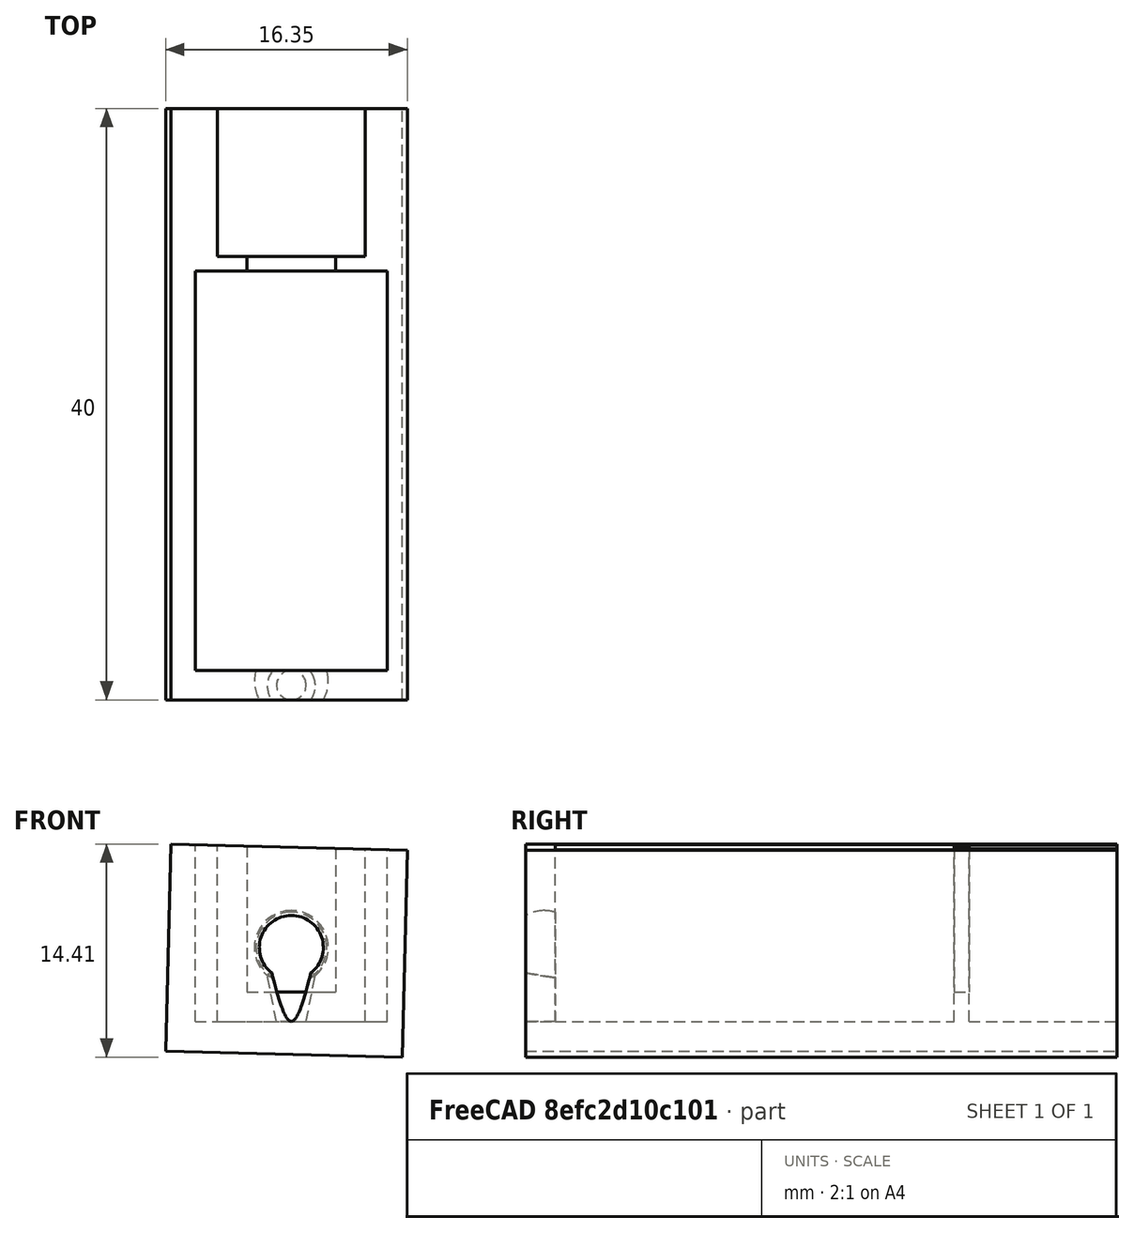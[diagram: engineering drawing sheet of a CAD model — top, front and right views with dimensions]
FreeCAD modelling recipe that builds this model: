
FCSTD DOCUMENT  (FreeCAD 0.16R4924 (Git))
Label: solenoid_bay
License: All rights reserved
LicenseURL: http://en.wikipedia.org/wiki/All_rights_reserved
objects: Part::Cut×5, Part::Box×4, Part::Sphere×1, Part::Cone×1
note: 11 computed .brp shape members not serialized (recipe doc carries the construction recipe); baked Part::Feature solids carry a one-line shape summary decoded from their .brp

FEATURE [Part::Box] Box  label="Case"
  Height = 14
  Length = 16
  Placement = pos=(0,0,0) rot=(0,1,0;0.025408rad)
  Width = 40
FEATURE [Part::Box] Box001  label="solenoidBay"
  Height = 12
  Length = 13
  Placement = pos=(2,2,2) rot=(0,0,1;0rad)
  Width = 27
FEATURE [Part::Cut] Cut
  Base = -> Box
  Tool = -> Box001
FEATURE [Part::Box] Box002  label="pullBay"
  Height = 15
  Length = 10
  Placement = pos=(3.5,30,2) rot=(0,0,1;0rad)
  Width = 10
FEATURE [Part::Cut] Cut001
  Base = -> Cut
  Tool = -> Box002
FEATURE [Part::Box] Box003  label="neck"
  Height = 15
  Length = 6
  Placement = pos=(5.5,28,4) rot=(0,0,1;0rad)
  Width = 4
FEATURE [Part::Cut] Cut002
  Base = -> Cut001
  Tool = -> Box003
FEATURE [Part::Sphere] Sphere  label="pinhole"
  Angle1 = -90
  Angle2 = 90
  Angle3 = 360
  Placement = pos=(8.5,1.25,7) rot=(0,0,1;0rad)
  Radius = 2.5
FEATURE [Part::Cut] Cut003
  Base = -> Cut002
  Tool = -> Sphere
FEATURE [Part::Cone] Cone
  Angle = 360
  Height = 5
  Placement = pos=(8.5,1,2) rot=(0,0,1;0rad)
  Radius1 = 1
  Radius2 = 2
FEATURE [Part::Cut] Cut004
  Base = -> Cut003
  Tool = -> Cone
